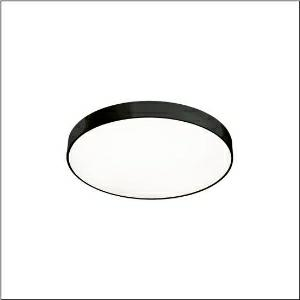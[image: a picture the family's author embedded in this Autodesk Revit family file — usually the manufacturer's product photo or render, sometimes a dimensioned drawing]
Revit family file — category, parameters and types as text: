
# Revit family: round_21_m_51mr36gm8321b
name_source: partatom
category: Lighting Fixtures
units: mm (PartAtom-declared; Revit-internal decimal feet)

## family parameters
Cut with Voids When Loaded = No
Host = Face
Light Source = No
Part Type = Normal
Room Calculation Point = No
Round Connector Dimension = Use Diameter
Shared = No

## types (1)
- --- (1 x LED, 8610 lm, 62.3 W, 3000K)
    Apparent Load = 62 VA
    CIE Flux Codes = 49 80 96 85 100
    Color Rendering = 80
    Color Temperature = 3000K
    Default Elevation = 1800 mm
    Description = Round 21 M, wall and ceiling luminaire, primary optical cover: cover, of PMMA, opal, light emission: direct/indirect distribution, primary light characteristic: symmetric, installation type: suspended mounting, surface-mounted, LED, rated luminous flux: 8.600lm, luminous efficacy: 138lm/W, light colour: 830, colour temperature: 3000K, control gear: ON/OFF Multilumen, with terminal, 3-pole, mains connection: 230V, AC, 50/60Hz, rated input power: 62.3W, housing, of aluminium, coated, black, diameter: 600mm, height: 62mm, protection rating (complete): IP40, insulation class (complete): insulation class I (protective earthing), certification: CE, impact resistance: IK04, permissible operating ambient temperature: -10..+35°C, packaging unit: 1 piece
    Height = 87 mm
    Lamp = 1 x LED
    Lamp Light Flux = 8610 lm
    Lamp Power = 62.3 W
    Lamp count = 1
    Length = 600 mm
    Luminous efficacy = 138 lm/W
    Manufacturer = Siteco
    ModVariant = No
    Model = 51MR36GM8321B
    Mounting Place = Ceiling
    Mounting Type = Surface mounted
    Number of Poles = 1
    OnlyDefault = Yes
    Power Factor = 1
    Product Name = Round 21 M
    Product group = wall and ceiling luminaire
    ProductGroupID = 304
    Protection Class = Protection class I
    Protection Degree = IP 40
    RLX_Detail_Level = 1
    RLX_Emergency_Light_Flux = 0 lm
    RLX_Emergency_Type = 0
    RLX_Emergency_Type_DB = No
    RlxData = <blob elided: 20821 chars, md5=79738a35>
    Socket = socket
    Standby Power = 0 W
    System Light Flux = 8610 lm
    System Power = 62 W
    Type Comments = factory setting: luminous flux: 100 % | (ON | ON | ON | ON) | 700 mA
    Type Image = l_1258332.jpg
    URL = http://relux.com
    VarID = @adj_033018
    Voltage = 0 V
    Weight = 0.00 kg
    Width = 0 mm  [stored 0 ft]

note: [stored X ft] marks values corroborated as IEEE doubles in the binary element streams (Revit-internal decimal feet)

## geometry (parser evidence)
native form markers: Blend x4, Sweep x15
no freeform markers — native parametric forms only
